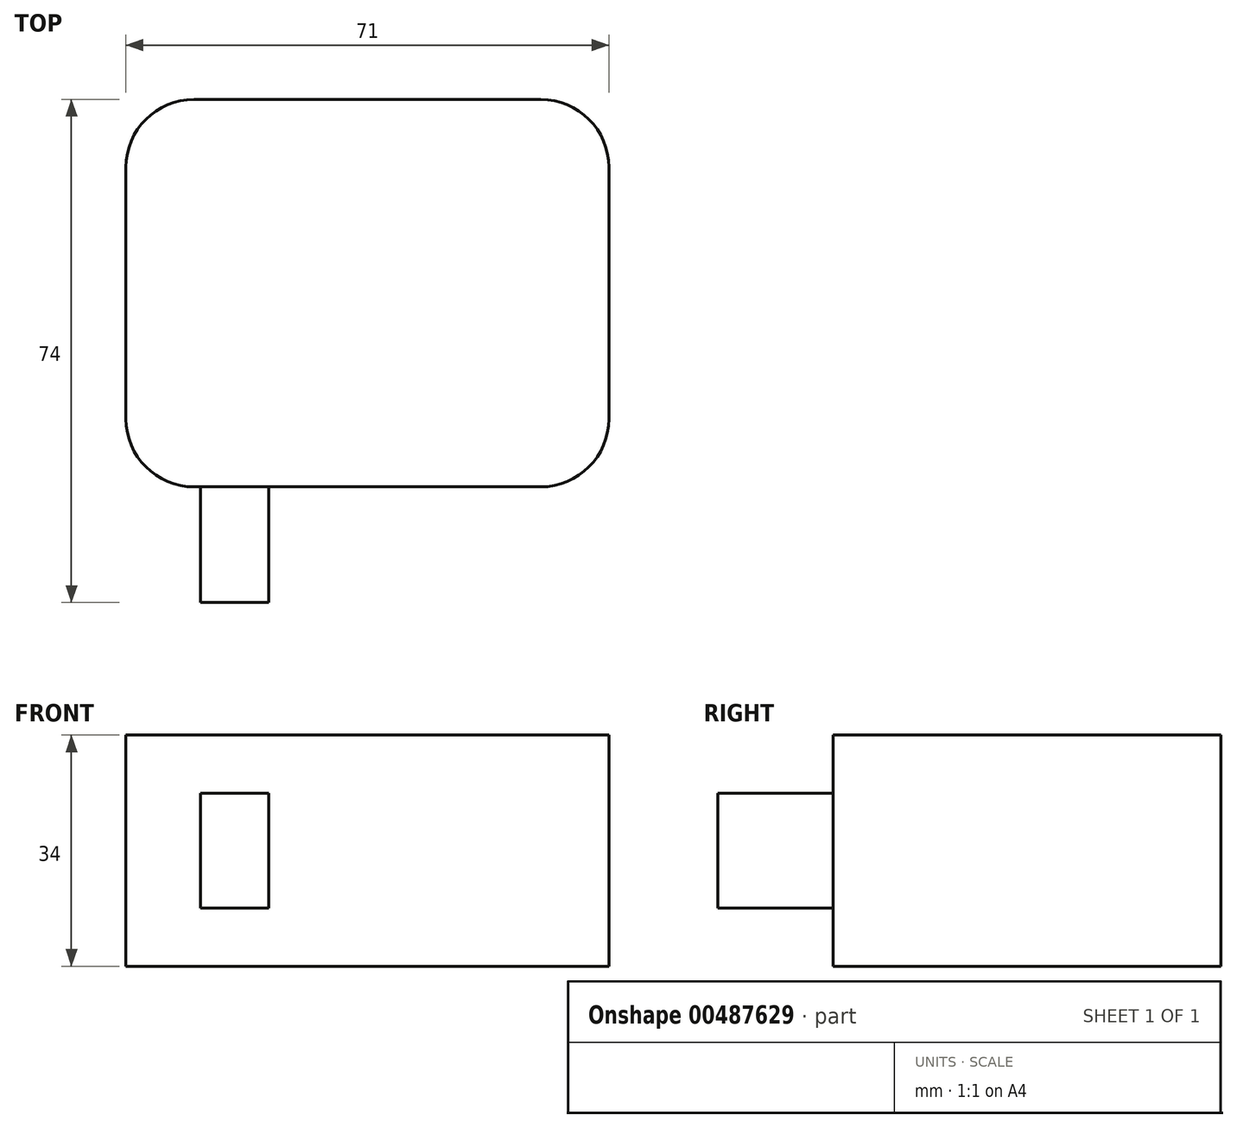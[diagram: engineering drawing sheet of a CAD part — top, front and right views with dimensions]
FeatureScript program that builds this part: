
annotation { "Feature Type Name" : "Feature", "Feature Type Description" : "" }
export const myFeature = defineFeature(function(context is Context, id is Id, definition is map)
    precondition{}
    {
        {
            var Q0;
            Q0=qCreatedBy(makeId("Top.planeOp"),FACE);
            var sketch = newSketch(context, id + "F0", { "sketchPlane" : qUnion([Q0])});
            skLineSegment(sketch, "E0.bottom", {"start": v(35.5, -28.5) * mm, "end": v(-35.5, -28.5) * mm});
            skLineSegment(sketch, "E0.top", {"start": v(35.5, 28.5) * mm, "end": v(-35.5, 28.5) * mm});
            skLineSegment(sketch, "E0.left", {"start": v(35.5, -28.5) * mm, "end": v(35.5, 28.5) * mm});
            skLineSegment(sketch, "E0.right", {"start": v(-35.5, -28.5) * mm, "end": v(-35.5, 28.5) * mm});
            skPoint(sketch, "E0.middle", {"position": v(0, 0) * mm});
            skSolve(sketch);
        }
        {
            var Q0;
            Q0 = qSketchRegion(id + "F0", true);
            extrude(context, id + "F1", {"entities" : qUnion([Q0]), "depth" : 34 * mm});
        }
        {
            var Q0;
            Q0=makeQuery(id+"F1.opExtrude","SWEPT_EDGE",EDGE,{"disambiguationData":[OSD([sQuery(id+"F0.wireOp",EDGE,"E0.top"),sQuery(id+"F0.wireOp",EDGE,"E0.right")])]});
            var Q1;
            Q1=makeQuery(id+"F1.opExtrude","SWEPT_EDGE",EDGE,{"disambiguationData":[OSD([sQuery(id+"F0.wireOp",EDGE,"E0.top"),sQuery(id+"F0.wireOp",EDGE,"E0.left")])]});
            var Q2;
            Q2=makeQuery(id+"F1.opExtrude","SWEPT_EDGE",EDGE,{"disambiguationData":[OSD([sQuery(id+"F0.wireOp",EDGE,"E0.bottom"),sQuery(id+"F0.wireOp",EDGE,"E0.right")])]});
            var Q3;
            Q3=makeQuery(id+"F1.opExtrude","SWEPT_EDGE",EDGE,{"disambiguationData":[OSD([sQuery(id+"F0.wireOp",EDGE,"E0.bottom"),sQuery(id+"F0.wireOp",EDGE,"E0.left")])]});
            fillet(context, id + "F2", {"entities" : qUnion([Q0, Q1, Q2, Q3]), "radius" : 10 * mm, "tangentPropagation" : true, "allowEdgeOverflow" : false});
        }
        {
            var Q0;
            Q0=makeQuery(id+"F1.opExtrude","SWEPT_FACE",FACE,{"disambiguationData":[OSD([sQuery(id+"F0.wireOp",EDGE,"E0.bottom")])]});
            var sketch = newSketch(context, id + "F3", { "sketchPlane" : qUnion([Q0])});
            skLineSegment(sketch, "E1.bottom", {"start": v(-14.48, 8.53) * mm, "end": v(-24.52, 8.53) * mm});
            skLineSegment(sketch, "E1.top", {"start": v(-14.48, 25.47) * mm, "end": v(-24.52, 25.47) * mm});
            skLineSegment(sketch, "E1.left", {"start": v(-14.48, 8.53) * mm, "end": v(-14.48, 25.47) * mm});
            skLineSegment(sketch, "E1.right", {"start": v(-24.52, 8.53) * mm, "end": v(-24.52, 25.47) * mm});
            skPoint(sketch, "E1.middle", {"position": v(-19.5, 17) * mm});
            skPoint(sketch, "E1.middle.positionSnap0", {"position": v(-25.5, 17) * mm});
            skPoint(sketch, "E1.centerSnap0", {"position": v(-25.5, 17) * mm});
            skSolve(sketch);
        }
        {
            var Q0;
            Q0 = qSketchRegion(id + "F3", true);
            extrude(context, id + "F4", {"entities" : qUnion([Q0]), "operationType" : NewBodyOperationType.ADD, "depth" : 17 * mm});
        }
    });
